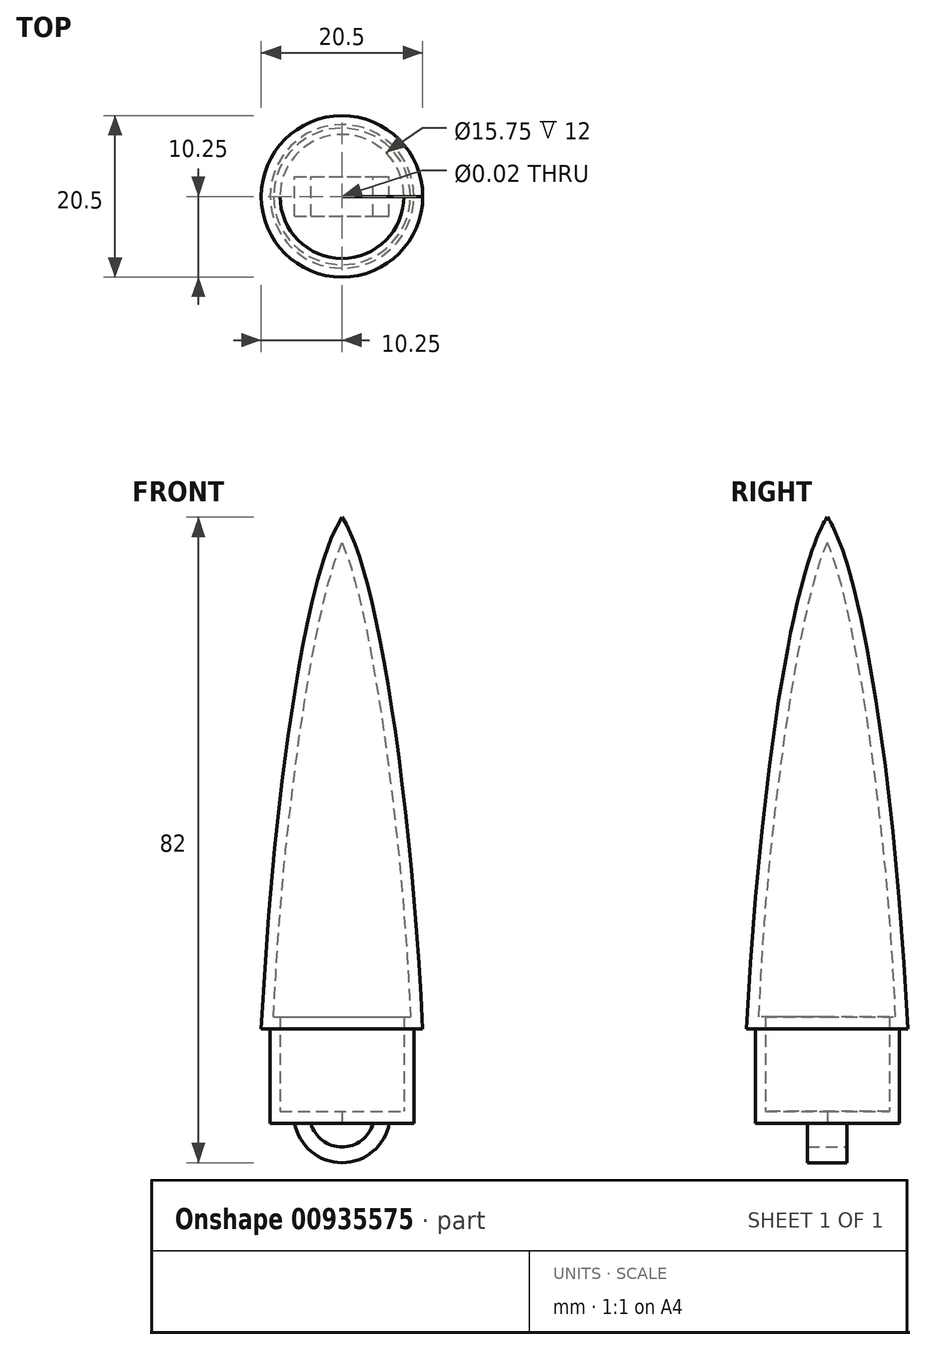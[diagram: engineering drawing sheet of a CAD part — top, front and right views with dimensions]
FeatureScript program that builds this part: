
annotation { "Feature Type Name" : "Feature", "Feature Type Description" : "" }
export const myFeature = defineFeature(function(context is Context, id is Id, definition is map)
    precondition{}
    {
        {
            var Q0;
            Q0=qCreatedBy(makeId("Front.planeOp"),FACE);
            var sketch = newSketch(context, id + "F0", { "sketchPlane" : qUnion([Q0])});
            skLineSegment(sketch, "E0", {"start": v(0, 0) * mm, "end": v(0, 65) * mm});
            skLineSegment(sketch, "E1", {"start": v(0, 0) * mm, "end": v(10.25, 0) * mm});
            skFitSpline(sketch, "E2", {"points": [v(0, 65) * mm, v(10.25, 0) * mm], "startDerivative": vector(12.7, -18.7) * mm, "endDerivative": vector(5.05, -97.5) * mm});
            skPoint(sketch, "E3", {"position": v(5.12, 32.5) * mm});
            skFitSpline(sketch, "E4.0", {"points": [v(-1.24, 64.16) * mm, v(-1.03, 63.84) * mm, v(-0.56, 63.03) * mm, v(0.43, 60.71) * mm, v(1.7, 56.67) * mm, v(3.2, 50.2) * mm, v(4.62, 42.32) * mm, v(5.92, 33.2) * mm, v(7.46, 19.6) * mm, v(8.33, 8.02) * mm, v(8.75, -0.08) * mm]});
            skLineSegment(sketch, "E5.bottom", {"start": v(7.88, 1.5) * mm, "end": v(9.12, 1.5) * mm});
            skLineSegment(sketch, "E5.top", {"start": v(7.88, -12) * mm, "end": v(9.12, -12) * mm});
            skLineSegment(sketch, "E5.left", {"start": v(7.88, 1.5) * mm, "end": v(7.88, -12) * mm});
            skLineSegment(sketch, "E5.right", {"start": v(9.12, 1.5) * mm, "end": v(9.12, -12) * mm});
            skLineSegment(sketch, "E6.bottom", {"start": v(0.01, -10.5) * mm, "end": v(7.88, -10.5) * mm});
            skLineSegment(sketch, "E6.top", {"start": v(0.01, -12) * mm, "end": v(7.88, -12) * mm});
            skLineSegment(sketch, "E6.left", {"start": v(0.01, -10.5) * mm, "end": v(0.01, -12) * mm});
            skLineSegment(sketch, "E6.right", {"start": v(7.88, -10.5) * mm, "end": v(7.88, -12) * mm});
            skSolve(sketch);
        }
        {
            var Q0;
            Q0=makeQuery(id+"F0.imprint","IMPRINT",FACE,{"disambiguationData":[TD([[makeQuery(id+"F0.imprint","IMPRINT",EDGE,{"derivedFrom":sQuery(id+"F0.wireOp",EDGE,"E6.bottom")}),-1.0]])]});
            var Q1;
            {var subQ0=sQuery(id+"F0.wireOp",EDGE,"E5.top");Q1=makeQuery(id+"F0.imprint","IMPRINT",FACE,{"disambiguationData":[TD([[makeQuery(id+"F0.imprint","IMPRINT",EDGE,{"derivedFrom":subQ0}),1.0]])]});}
            var Q2;
            {var subQ0=sQuery(id+"F0.wireOp",EDGE,"E4.0");var subQ1=sQuery(id+"F0.wireOp",EDGE,"E1");var subQ2=makeQuery(id+"F0.imprint","INTERSECT",VERTEX,{"derivedFrom":[subQ1,subQ0]});Q2=makeQuery(id+"F0.imprint","IMPRINT",FACE,{"disambiguationData":[TD([[makeQuery(id+"F0.imprint","IMPRINT",EDGE,{"disambiguationData":[TD([[subQ2,-1.0]])],"derivedFrom":subQ1}),1.0]])]});}
            var Q3;
            {var subQ0=sQuery(id+"F0.wireOp",EDGE,"E5.left");var subQ1=sQuery(id+"F0.wireOp",EDGE,"E1");var subQ2=makeQuery(id+"F0.imprint","INTERSECT",VERTEX,{"derivedFrom":[subQ1,subQ0]});Q3=makeQuery(id+"F0.imprint","IMPRINT",FACE,{"disambiguationData":[TD([[makeQuery(id+"F0.imprint","IMPRINT",EDGE,{"disambiguationData":[TD([[subQ2,-1.0]])],"derivedFrom":subQ1}),1.0]])]});}
            var Q4;
            {var subQ5=sQuery(id+"F0.wireOp",EDGE,"E2");Q4=makeQuery(id+"F0.imprint","IMPRINT",FACE,{"disambiguationData":[TD([[makeQuery(id+"F0.imprint","IMPRINT",EDGE,{"derivedFrom":subQ5}),-1.0]])]});}
            var Q5;
            Q5=sQuery(id+"F0.wireOp",EDGE,"E0");
            revolve(context, id + "F1", {"surfaceOperationType" : NewSurfaceOperationType.NEW, "entities" : qUnion([Q0, Q1, Q2, Q3, Q4]), "axis" : qUnion([Q5]), "revolveType" : RevolveType.FULL});
        }
        {
            var Q0;
            Q0=qCreatedBy(makeId("Front.planeOp"),FACE);
            var sketch = newSketch(context, id + "F2", { "sketchPlane" : qUnion([Q0])});
            skArc(sketch, "E7", {"start": v(-6, -12) * mm, "mid": v(0, -17) * mm, "end": v(6, -12) * mm});
            skArc(sketch, "E8.0", {"start": v(-3.95, -12) * mm, "mid": v(0, -15) * mm, "end": v(3.95, -12) * mm});
            skLineSegment(sketch, "E9", {"start": v(-6, -12) * mm, "end": v(6, -12) * mm});
            skSolve(sketch);
        }
        {
            var Q0;
            {var subQ0=sQuery(id+"F2.wireOp",EDGE,"E7");Q0=makeQuery(id+"F2.imprint","IMPRINT",FACE,{"disambiguationData":[TD([[makeQuery(id+"F2.imprint","IMPRINT",EDGE,{"derivedFrom":subQ0}),1.0]])]});}
            extrude(context, id + "F3", {"entities" : qUnion([Q0]), "operationType" : NewBodyOperationType.ADD, "endBound" : BoundingType.SYMMETRIC, "depth" : 5 * mm, "offsetDistance" : 25 * mm});
        }
    });
